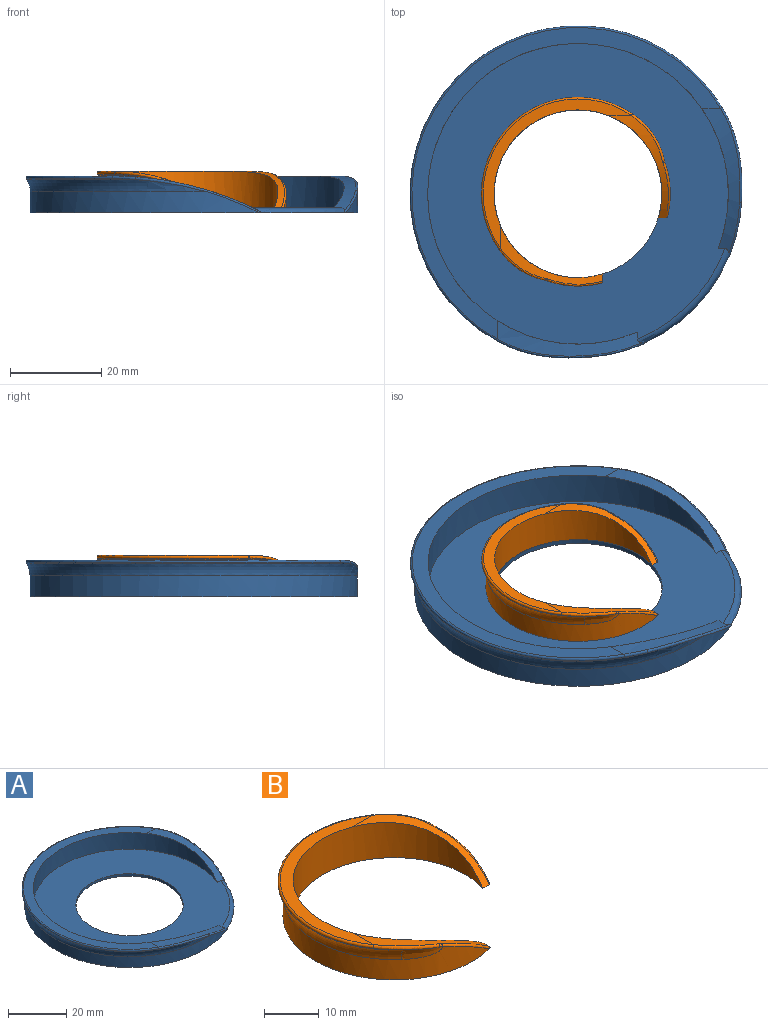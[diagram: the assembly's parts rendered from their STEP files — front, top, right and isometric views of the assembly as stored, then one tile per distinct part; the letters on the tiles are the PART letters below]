
ASSEMBLY  parts=2 mates=1
PART A: 18 faces, bbox 81x81x10.6 mm
  f0: cylinder r=35.95mm len=71.91mm, axis (0,0,1), area 844mm2, adj f3,f8,f9,f13
  f1: plane 68.36x67.78mm, normal (0,0,1), area 434.8mm2, adj f5,f6,f7,f12
  f2: cone r=37.22mm half-angle=32deg, axis (0,0,1), area 28.9mm2, adj f8,f11,f12,f14
  f3: plane 71.92x71.92mm, normal (0,0,-1), area 2993.3mm2, adj f0,f9,f13,f16,f17
  f4: plane 66.04x66.04mm, normal (0,0,1), area 2398.5mm2, adj f5,f6,f7,f16,f17
  f5: cylinder r=33.02mm len=66.04mm, axis (0,0,1), area 1045.1mm2, adj f1,f4,f6,f7
  f6: cylinder r=71.12mm len=31.94mm, axis (-1,0,0), area 92mm2, adj f1,f4,f5,f13,f14,f15,f16
  f7: cylinder r=71.12mm len=31.95mm, axis (0,1,0), area 91.7mm2, adj f1,f4,f5,f9,f10,f11,f16
  f8: torus R=41.03mm, axis (0,0,1), area 452.5mm2, adj f0,f2,f10,f15
  f9: bspline ~19.6x8.36mm, area 7.7mm2, adj f0,f3,f7,f10,f16
  f10: bspline ~23.63x4.58mm, area 12.7mm2, adj f7,f8,f9,f11
  f11: bspline ~11.71x5.92mm, area 4.8mm2, adj f2,f7,f10,f12
  f12: torus R=36.49mm, axis (0,0,1), area 116.6mm2, adj f1,f2,f11,f14
  f13: bspline ~16.69x6.72mm, area 7.7mm2, adj f0,f3,f6,f15,f16
  f14: bspline ~11.62x6.29mm, area 4.9mm2, adj f2,f6,f12,f15
  f15: bspline ~23.47x5.09mm, area 12.8mm2, adj f6,f8,f13,f14
  f16: torus R=34.43mm, axis (0,0,1), area 53.1mm2, adj f3,f4,f6,f7,f9,f13
  f17: cylinder r=18.41mm len=36.83mm, axis (0,0,1), area 117.6mm2, adj f3,f4
PART B: 17 faces, bbox 44x44x10.7 mm
  f0: cylinder r=20.28mm len=40.56mm, axis (0,0,1), area 453mm2, adj f1,f7,f9,f13,f14,f15
  f1: plane 40.69x40.69mm, normal (0,0,-1), area 190.4mm2, adj f0,f4,f5,f6,f7,f9
  f2: plane 32.72x32.53mm, normal (0,0,1), area 121.5mm2, adj f4,f5,f6,f10
  f3: cone r=21.55mm half-angle=32deg, axis (0,0,1), area 13.2mm2, adj f8,f10,f11,f14
  f4: cylinder r=18.41mm len=36.83mm, axis (0,0,1), area 563.1mm2, adj f1,f2,f5,f6
  f5: cylinder r=35.56mm len=22.5mm, axis (0,-1,0), area 50.4mm2, adj f1,f2,f4,f9,f11
  f6: cylinder r=35.56mm len=22.5mm, axis (-1,0,0), area 50.7mm2, adj f1,f2,f4,f7,f8
  f7: bspline ~16.32x9.36mm, area 8.8mm2, adj f0,f1,f6,f16
  f8: bspline ~13.58x9.86mm, area 11mm2, adj f3,f6,f10,f15,f16
  f9: bspline ~15.62x8.55mm, area 8.8mm2, adj f0,f1,f5,f12
  f10: torus R=20.82mm, axis (0,0,1), area 50.7mm2, adj f2,f3,f8,f11
  f11: bspline ~13.62x9.7mm, area 10.9mm2, adj f3,f5,f10,f12,f13
  f12: bspline ~0.7x0.61mm, area 0.2mm2, adj f9,f11,f13
  f13: bspline ~7.62x4.23mm, area 15.9mm2, adj f0,f11,f12,f14
  f14: torus R=25.36mm, axis (0,0,1), area 190.8mm2, adj f0,f3,f13,f15
  f15: bspline ~8.88x5.51mm, area 16mm2, adj f0,f8,f14,f16
  f16: bspline ~0.7x0.6mm, area 0.2mm2, adj f7,f8,f15
PLACE A at identity
PLACE B t=(0,15.67,1.02)mm
MATE fastened B.f4 <-> A.f0  axis (0,0,-1) through (0,21.3,1.02)mm
